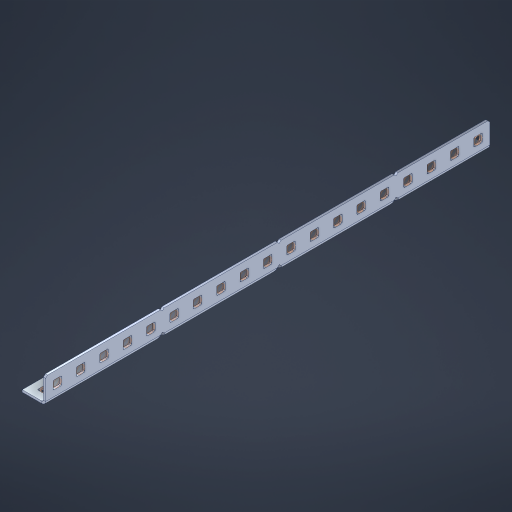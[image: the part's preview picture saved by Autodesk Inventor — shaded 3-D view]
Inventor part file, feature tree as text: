
AUTODESK INVENTOR PART (.ipt)
format: ipt  version: 2023 (Build 270158000, 158)  size: 726,528 bytes
history: native  units: in
note: dims shown in document units (in); Inventor stores cm internally (conversion verified against a paired STEP export)
features: other x43, extrude x37, sheet_metal_op x10, sketch x8, mirror x1, pattern_linear x1, chamfer x1
ambient origin geometry x8: Origin, YZ Plane, XZ Plane, XY Plane, X Axis, Y Axis, Z Axis, Center Point
bodies: Solid1 (feature_tree), Body (feature_tree)
feature tree (101):
  other  "Flange Pattern Plane"
  sheet_metal_op  "Flange Pattern"
  sheet_metal_op  "Body Pattern"
  other  "Arc Length"
  mirror  "Notch Mirror"
  pattern_linear  "Notch Pattern"  Spacing1=0.1875in  [1 undecoded]
  chamfer  "End Chamfer"
  extrude  "Half Cut"  Depth=0.0469in
  sketch  "Sketch1"  dims[d0=2.5in]
  other  "Plate1"
  sketch  "Sketch2"  dims[d1=9.5in]
  other  "Plate2"
  sheet_metal_op  "Bend1"
  sheet_metal_op  "Corner1"
  sketch  "Sketch3"  dims[d2=0.0469in]
  other  "Flange Pattern Sketch"
  sketch  "Sketch7"  dims[d3=0.0469in]
  other  "Srf1"
  other  "Srf2"
  sketch  "Sketch8"  dims[d4=0.0234in]
  sketch  "Sketch9"  dims[d5=0.0938in]
  other  "Srf91"
  sheet_metal_op  "Body Pattern Sketch"
  other  "Srf92"
  sketch  "Sketch13"  dims[d6=0.0469in]
  sketch  "Sketch14"  dims[d7=0.5in d8=90.0deg d9=0.0312in d10=0.1875in d11=0.0469in d12=0.0469in d16=0.182in d17=0.02in d18=0.0469in d19=0.0in d20=0.25in d21=0.25in d46=0.172in d47=1.0in d48=0.0in d49=0.182in d50=0.02in d51=0.25in d52=0.25in d53=0.0469in d54=0.0in d55=0.172in d56=1.0in d57=0.0in d60=7.4803in d62=0.5in d63=0.3937in d65=0.5in d85=0.1227in d86=0.1659in d88=0.04in d89=0.0469in d90=0.0in d91=0.04in d92=0.0491in d95=2.5in d96=0.04in d97=0.25in d98=45.0deg d101=0.0in d102=2.497in d131=0.5in d132=7.4803in d134=0.5in d139=0.5in]
  other  "Srf856"
  other  "Srf1310"
  other  "Srf1311"
  other  "Srf1312"
  other  "Srf1376"
  other  "Srf1377"
  other  "Srf1728"
  other  "Srf1755"
  other  "Srf1878"
  other  "Srf1879"
  other  "Srf1880"
  other  "Srf1881"
  other  "Srf1882"
  other  "Srf1883"
  other  "Srf1884"
  other  "Srf1885"
  other  "Srf1886"
  other  "Srf1887"
  other  "Srf1888"
  other  "Srf1889"
  other  "Srf1890"
  other  "Srf1942"
  other  "Srf1943"
  other  "Srf1944"
  other  "Srf1945"
  other  "Srf1946"
  other  "Srf1947"
  other  "Srf1948"
  other  "Srf1949"
  other  "Srf1950"
  other  "Srf1951"
  other  "Srf1952"
  other  "Srf1953"
  other  "Srf1954"
  sheet_metal_op  "Flange Stamp"
  sheet_metal_op  "Flange Circle"
  sheet_metal_op  "Body Stamp"
  sheet_metal_op  "Body Circle"
  sheet_metal_op  "Notch"
  extrude  "ExtrusionSrf2"  Depth=0.0469in
  extrude  "ExtrusionSrf92"  Depth=0.5in
  extrude  "ExtrusionSrf856"  Depth=0.02in
  extrude  "ExtrusionSrf1310"  Depth=0.0469in
  extrude  "ExtrusionSrf1311"  TaperAngle=0.0deg  [1 undecoded]
  extrude  "ExtrusionSrf1312"  Depth=0.5in
  extrude  "ExtrusionSrf1376"  Depth=0.5in
  extrude  "ExtrusionSrf1377"  Depth=0.5in
  extrude  "ExtrusionSrf1728"  Depth=0.5in TaperAngle=0.0deg
  extrude  "ExtrusionSrf1755"  Depth=0.5in
  extrude  "ExtrusionSrf1878"  Depth=0.02in
  extrude  "ExtrusionSrf1879"  Depth=0.5in
  extrude  "ExtrusionSrf1880"  Depth=0.5in
  extrude  "ExtrusionSrf1881"  Depth=0.0469in
  extrude  "ExtrusionSrf1882"  TaperAngle=0.0deg  [1 undecoded]
  extrude  "ExtrusionSrf1883"  Depth=0.5in
  extrude  "ExtrusionSrf1884"  Depth=0.5in TaperAngle=0.0deg
  extrude  "ExtrusionSrf1885"  Depth=0.5in
  extrude  "ExtrusionSrf1886"  Depth=0.5in
  extrude  "ExtrusionSrf1887"  Depth=0.5in
  extrude  "ExtrusionSrf1888"  Depth=0.5in
  extrude  "ExtrusionSrf1889"  Depth=0.5in
  extrude  "ExtrusionSrf1890"  Depth=0.0469in
  extrude  "ExtrusionSrf1942"  TaperAngle=0.0deg  [1 undecoded]
  extrude  "ExtrusionSrf1943"  Depth=0.5in
  extrude  "ExtrusionSrf1944"  Depth=0.5in
  extrude  "ExtrusionSrf1945"  Depth=0.5in
  extrude  "ExtrusionSrf1946"  Depth=0.5in TaperAngle=45.0deg
  extrude  "ExtrusionSrf1947"  TaperAngle=0.0deg  [1 undecoded]
  extrude  "ExtrusionSrf1948"  Depth=0.5in
  extrude  "ExtrusionSrf1949"  Depth=0.5in
  extrude  "ExtrusionSrf1950"  Depth=0.5in
  extrude  "ExtrusionSrf1951"  Depth=0.5in
  extrude  "ExtrusionSrf1952"  Depth=0.5in
  extrude  "ExtrusionSrf1953"  [1 undecoded]
  extrude  "ExtrusionSrf1954"  [1 undecoded]
note: 7 required parameter values undecoded (feature->parameter linkage not recoverable at this tier; creation-order binding heuristic only, values carry confidence <= 0.55)
